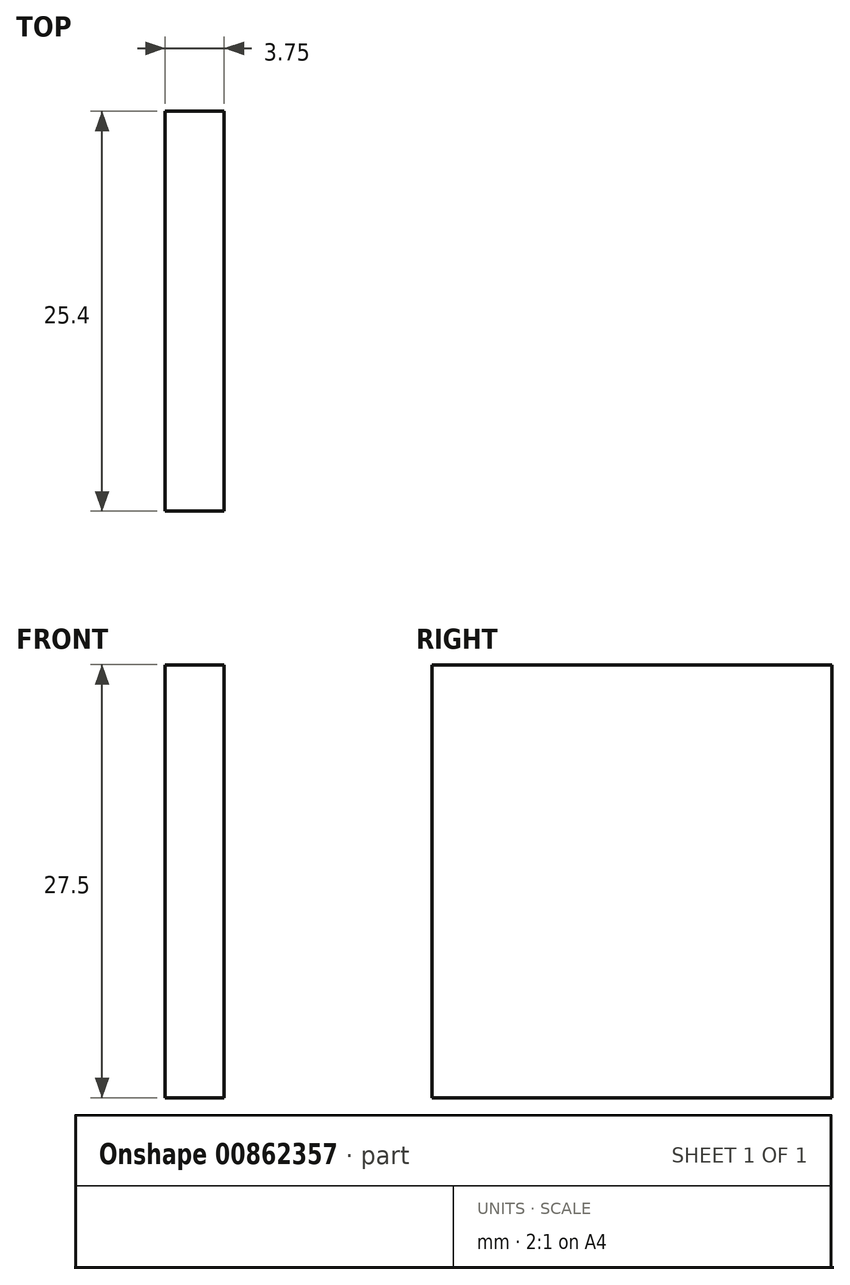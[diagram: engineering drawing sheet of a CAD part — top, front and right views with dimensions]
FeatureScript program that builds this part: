
annotation { "Feature Type Name" : "Feature", "Feature Type Description" : "" }
export const myFeature = defineFeature(function(context is Context, id is Id, definition is map)
    precondition{}
    {
        {
            var Q0;
            Q0=qCreatedBy(makeId("Front.planeOp"),FACE);
            var sketch = newSketch(context, id + "F0", { "sketchPlane" : qUnion([Q0])});
            skLineSegment(sketch, "E0.bottom", {"start": v(-7.95, -2.28) * mm, "end": v(-11.7, -2.28) * mm});
            skLineSegment(sketch, "E0.top", {"start": v(-7.95, 25.22) * mm, "end": v(-11.7, 25.22) * mm});
            skLineSegment(sketch, "E0.left", {"start": v(-7.95, -2.28) * mm, "end": v(-7.95, 25.22) * mm});
            skLineSegment(sketch, "E0.right", {"start": v(-11.7, -2.28) * mm, "end": v(-11.7, 25.22) * mm});
            skSolve(sketch);
        }
        {
            var Q0;
            Q0 = qSketchRegion(id + "F0", true);
            var sketch = newSketch(context, id + "F1", { "sketchPlane" : qUnion([Q0])});
            skSolve(sketch);
        }
        {
            var Q0;
            Q0 = qSketchRegion(id + "F0", true);
            var sketch = newSketch(context, id + "F2", { "sketchPlane" : qUnion([Q0])});
            skSolve(sketch);
        }
        {
            var Q0;
            Q0=makeQuery(id+"F2.imprint","IMPRINT",FACE,{"disambiguationData":[TD([[makeQuery(id+"F2.imprint","IMPRINT",EDGE,{"derivedFrom":makeQuery(id+"F0.imprint","IMPRINT",EDGE,{"derivedFrom":sQuery(id+"F0.wireOp",EDGE,"E0.bottom")})}),-1.0]])]});
            extrude(context, id + "F3", {"entities" : qUnion([Q0]), "depth" : 25.4 * mm, "offsetDistance" : 25.4 * mm});
        }
    });
